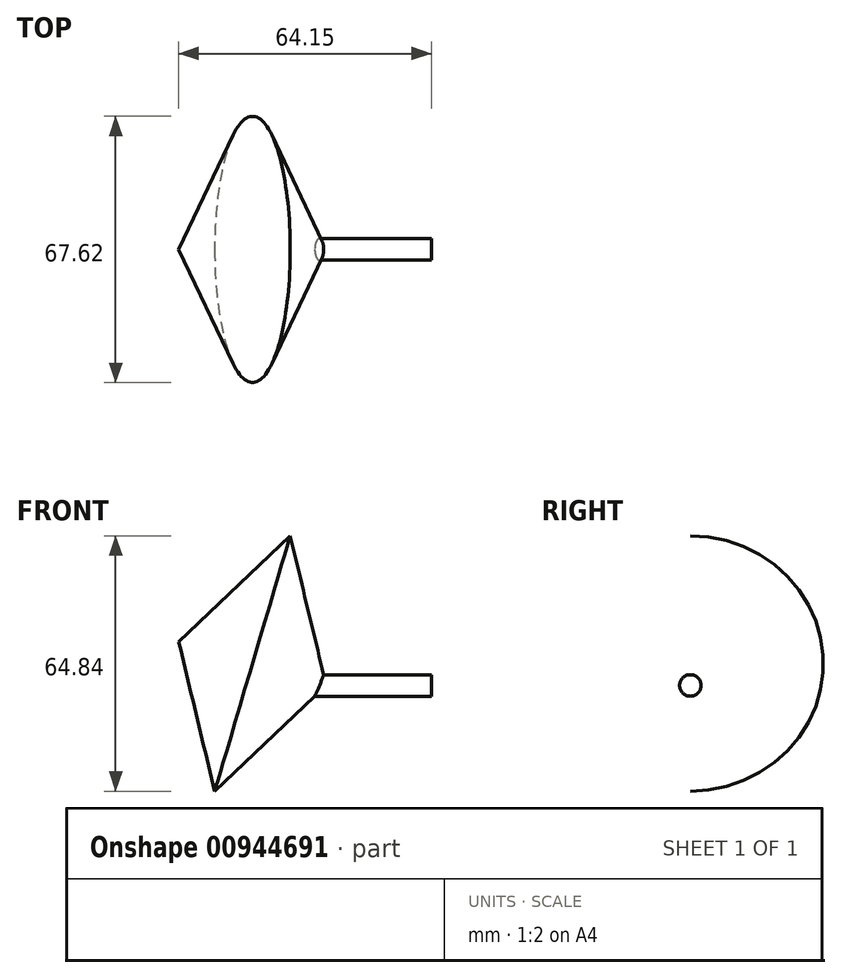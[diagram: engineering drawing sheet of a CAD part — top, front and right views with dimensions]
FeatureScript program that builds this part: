
annotation { "Feature Type Name" : "Feature", "Feature Type Description" : "" }
export const myFeature = defineFeature(function(context is Context, id is Id, definition is map)
    precondition{}
    {
        {
            var Q0;
            Q0=qCreatedBy(makeId("Front.planeOp"),FACE);
            var sketch = newSketch(context, id + "F0", { "sketchPlane" : qUnion([Q0])});
            skCircle(sketch, "E0.cCircle", {"center": v(-48.63, 8.17) * mm, "radius": 11.27 * mm, "construction": true});
            skLineSegment(sketch, "E0.0", {"start": v(-26.71, 13.44) * mm, "end": v(-55.03, -13.44) * mm});
            skLineSegment(sketch, "E0.1", {"start": v(-55.03, -13.44) * mm, "end": v(-64.15, 24.52) * mm});
            skLineSegment(sketch, "E0.2", {"start": v(-64.15, 24.52) * mm, "end": v(-26.71, 13.44) * mm});
            skPoint(sketch, "E0.0.midPoint", {"position": v(-40.87, 0) * mm});
            skSolve(sketch);
        }
        {
            var Q0;
            Q0 = qSketchRegion(id + "F0", true);
            var Q1;
            Q1=sQuery(id+"F0.wireOp",EDGE,"E0.2");
            revolve(context, id + "F1", {"surfaceOperationType" : NewSurfaceOperationType.NEW, "entities" : qUnion([Q0]), "axis" : qUnion([Q1]), "revolveType" : RevolveType.FULL});
        }
        {
            var Q0;
            Q0=qCreatedBy(makeId("Right.planeOp"),FACE);
            var sketch = newSketch(context, id + "F2", { "sketchPlane" : qUnion([Q0])});
            skCircle(sketch, "E1", {"center": v(0, 13.42) * mm, "radius": 2.74 * mm});
            skSolve(sketch);
        }
        {
            var Q0;
            Q0 = qSketchRegion(id + "F2", true);
            extrude(context, id + "F3", {"entities" : qUnion([Q0]), "operationType" : NewBodyOperationType.ADD, "oppositeDirection" : true, "depth" : 34 * mm, "offsetDistance" : 25.4 * mm});
        }
    });
